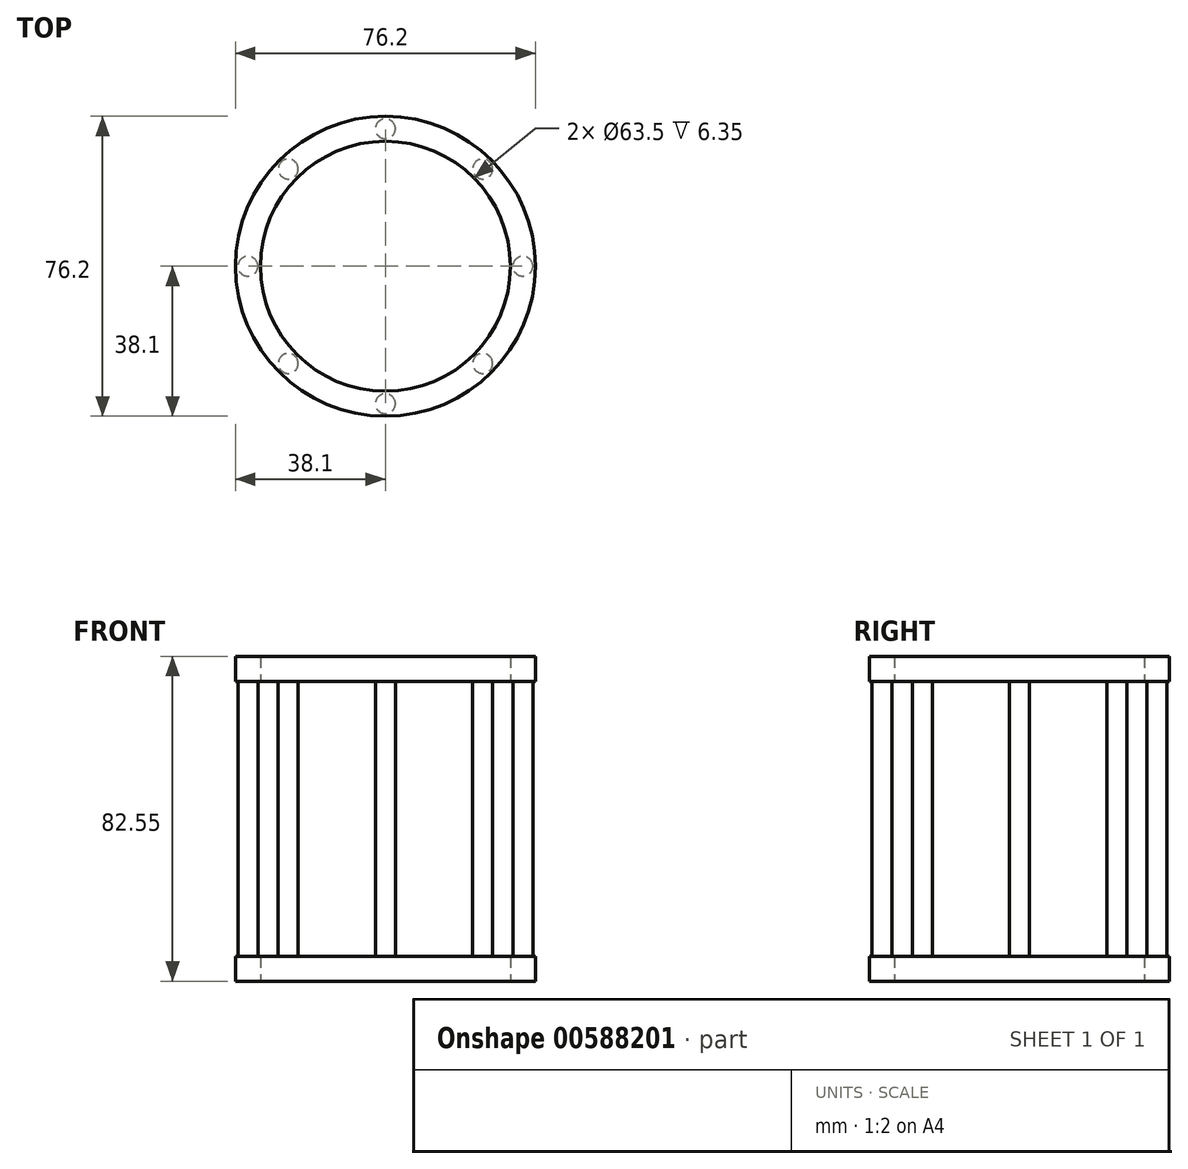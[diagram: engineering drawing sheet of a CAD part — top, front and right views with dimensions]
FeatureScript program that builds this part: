
annotation { "Feature Type Name" : "Feature", "Feature Type Description" : "" }
export const myFeature = defineFeature(function(context is Context, id is Id, definition is map)
    precondition{}
    {
        {
            var Q0;
            Q0=qCreatedBy(makeId("Top.planeOp"),FACE);
            var sketch = newSketch(context, id + "F0", { "sketchPlane" : qUnion([Q0])});
            skCircle(sketch, "E0", {"center": v(0, 0) * mm, "radius": 31.75 * mm});
            skCircle(sketch, "E1.0", {"center": v(0, 0) * mm, "radius": 38.1 * mm});
            skSolve(sketch);
        }
        {
            var Q0;
            Q0=makeQuery(id+"F0.imprint","IMPRINT",FACE,{"disambiguationData":[TD([[makeQuery(id+"F0.imprint","IMPRINT",EDGE,{"derivedFrom":sQuery(id+"F0.wireOp",EDGE,"E0")}),-1.0]])]});
            extrude(context, id + "F1", {"entities" : qUnion([Q0]), "depth" : 6.35 * mm, "offsetDistance" : 25.4 * mm});
        }
        {
            var Q0;
            Q0=makeQuery(id+"F1.opExtrude","CAP_FACE",FACE,{"disambiguationData":[OSD([sQuery(id+"F0.wireOp",EDGE,"E0"),sQuery(id+"F0.wireOp",EDGE,"E1.0")])],"isStart":false});
            var sketch = newSketch(context, id + "F2", { "sketchPlane" : qUnion([Q0])});
            skLineSegment(sketch, "E2", {"start": v(0, 31.75) * mm, "end": v(0, 38.1) * mm, "construction": true});
            skCircle(sketch, "E3", {"center": v(0, 34.92) * mm, "radius": 2.54 * mm});
            skCircle(sketch, "E4.1.0", {"center": v(-24.7, 24.7) * mm, "radius": 2.54 * mm});
            skCircle(sketch, "E4.2.0", {"center": v(-34.92, 0) * mm, "radius": 2.54 * mm});
            skCircle(sketch, "E4.3.0", {"center": v(-24.7, -24.7) * mm, "radius": 2.54 * mm});
            skCircle(sketch, "E4.4.0", {"center": v(0, -34.92) * mm, "radius": 2.54 * mm});
            skCircle(sketch, "E4.5.0", {"center": v(24.7, -24.7) * mm, "radius": 2.54 * mm});
            skCircle(sketch, "E4.6.0", {"center": v(34.92, 0) * mm, "radius": 2.54 * mm});
            skCircle(sketch, "E4.7.0", {"center": v(24.7, 24.7) * mm, "radius": 2.54 * mm});
            skPoint(sketch, "E4.center", {"position": v(0, 0) * mm});
            skSolve(sketch);
        }
        {
            var Q0;
            Q0=makeQuery(id+"F2.imprint","IMPRINT",FACE,{"disambiguationData":[TD([[makeQuery(id+"F2.imprint","IMPRINT",EDGE,{"derivedFrom":sQuery(id+"F2.wireOp",EDGE,"E4.7.0")}),1.0]])]});
            var Q1;
            Q1=makeQuery(id+"F2.imprint","IMPRINT",FACE,{"disambiguationData":[TD([[makeQuery(id+"F2.imprint","IMPRINT",EDGE,{"derivedFrom":sQuery(id+"F2.wireOp",EDGE,"E4.6.0")}),1.0]])]});
            var Q2;
            Q2=makeQuery(id+"F2.imprint","IMPRINT",FACE,{"disambiguationData":[TD([[makeQuery(id+"F2.imprint","IMPRINT",EDGE,{"derivedFrom":sQuery(id+"F2.wireOp",EDGE,"E4.5.0")}),1.0]])]});
            var Q3;
            Q3=makeQuery(id+"F2.imprint","IMPRINT",FACE,{"disambiguationData":[TD([[makeQuery(id+"F2.imprint","IMPRINT",EDGE,{"derivedFrom":sQuery(id+"F2.wireOp",EDGE,"E4.4.0")}),1.0]])]});
            var Q4;
            Q4=makeQuery(id+"F2.imprint","IMPRINT",FACE,{"disambiguationData":[TD([[makeQuery(id+"F2.imprint","IMPRINT",EDGE,{"derivedFrom":sQuery(id+"F2.wireOp",EDGE,"E4.3.0")}),1.0]])]});
            var Q5;
            Q5=makeQuery(id+"F2.imprint","IMPRINT",FACE,{"disambiguationData":[TD([[makeQuery(id+"F2.imprint","IMPRINT",EDGE,{"derivedFrom":sQuery(id+"F2.wireOp",EDGE,"E4.2.0")}),1.0]])]});
            var Q6;
            Q6=makeQuery(id+"F2.imprint","IMPRINT",FACE,{"disambiguationData":[TD([[makeQuery(id+"F2.imprint","IMPRINT",EDGE,{"derivedFrom":sQuery(id+"F2.wireOp",EDGE,"E4.1.0")}),1.0]])]});
            var Q7;
            Q7=makeQuery(id+"F2.imprint","IMPRINT",FACE,{"disambiguationData":[TD([[makeQuery(id+"F2.imprint","IMPRINT",EDGE,{"derivedFrom":sQuery(id+"F2.wireOp",EDGE,"E3")}),1.0]])]});
            extrude(context, id + "F3", {"entities" : qUnion([Q0, Q1, Q2, Q3, Q4, Q5, Q6, Q7]), "operationType" : NewBodyOperationType.ADD, "depth" : 69.85 * mm, "offsetDistance" : 25.4 * mm});
        }
        {
            var Q0;
            Q0=makeQuery(id+"F3.opExtrude","CAP_FACE",FACE,{"disambiguationData":[OSD([sQuery(id+"F2.wireOp",EDGE,"E3")])],"isStart":false});
            var sketch = newSketch(context, id + "F4", { "sketchPlane" : qUnion([Q0])});
            skCircle(sketch, "E5.0", {"center": v(0, 0) * mm, "radius": 38.1 * mm});
            skCircle(sketch, "E6.0", {"center": v(0, 0) * mm, "radius": 31.75 * mm});
            skSolve(sketch);
        }
        {
            var Q0;
            Q0=makeQuery(id+"F4.imprint","IMPRINT",FACE,{"disambiguationData":[TD([[makeQuery(id+"F4.imprint","IMPRINT",EDGE,{"derivedFrom":sQuery(id+"F4.wireOp",EDGE,"E5.0")}),1.0]])]});
            var Q1;
            Q1=makeQuery(id+"F4.imprint","IMPRINT",FACE,{"disambiguationData":[TD([[makeQuery(id+"F4.imprint","IMPRINT",EDGE,{"derivedFrom":makeQuery(id+"F3.opExtrude","CAP_EDGE",EDGE,{"disambiguationData":[OSD([sQuery(id+"F2.wireOp",EDGE,"E3")])],"isStart":false})}),1.0]])]});
            extrude(context, id + "F5", {"entities" : qUnion([Q0, Q1]), "operationType" : NewBodyOperationType.ADD, "depth" : 6.35 * mm, "offsetDistance" : 25.4 * mm});
        }
    });
